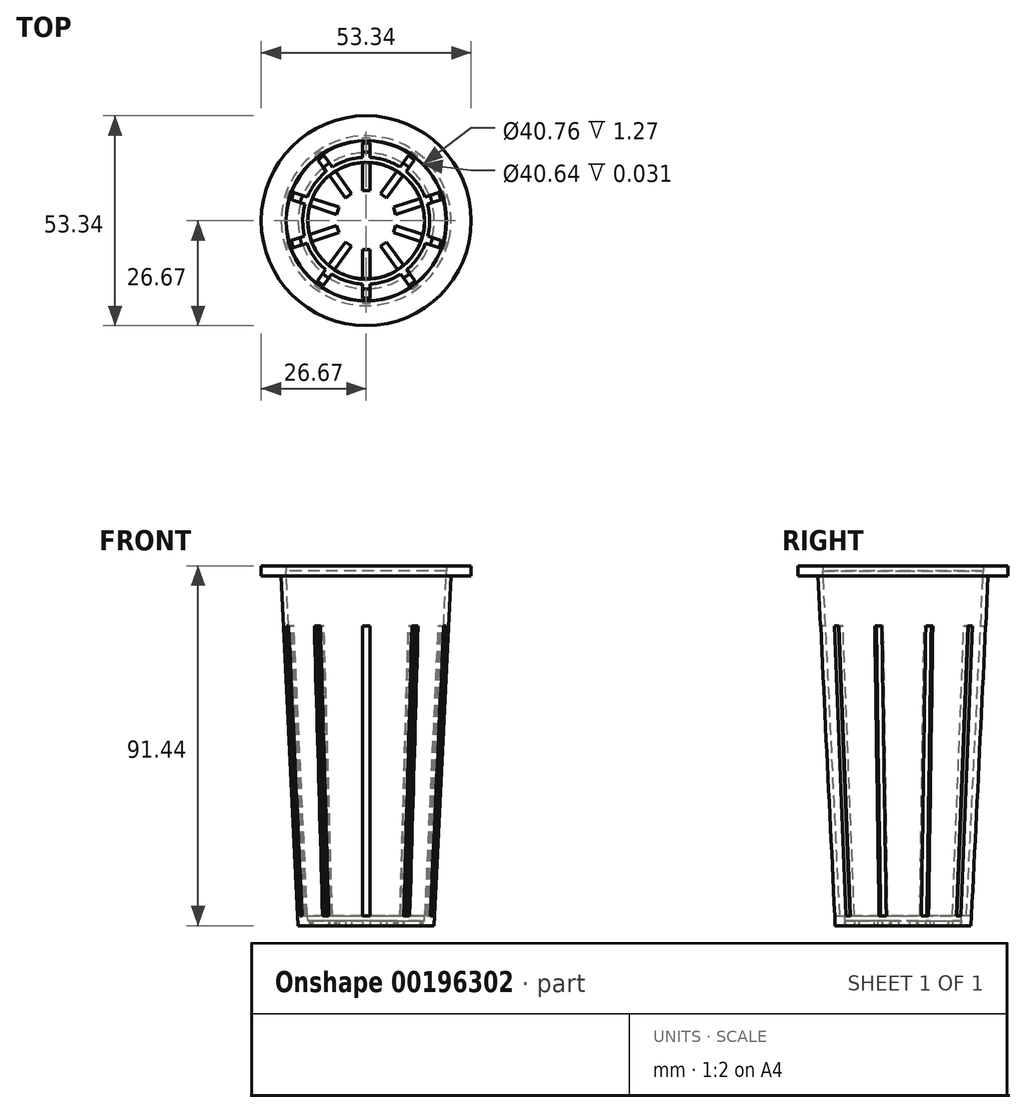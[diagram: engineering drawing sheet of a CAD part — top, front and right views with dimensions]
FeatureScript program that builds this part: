
annotation { "Feature Type Name" : "Feature", "Feature Type Description" : "" }
export const myFeature = defineFeature(function(context is Context, id is Id, definition is map)
    precondition{}
    {
        {
            var Q0;
            Q0=qCreatedBy(makeId("Front.planeOp"),FACE);
            var sketch = newSketch(context, id + "F0", { "sketchPlane" : qUnion([Q0])});
            skLineSegment(sketch, "E0", {"start": v(0, 0) * mm, "end": v(0, 88.9) * mm});
            skLineSegment(sketch, "E1", {"start": v(0, 88.9) * mm, "end": v(0, 91.44) * mm});
            skLineSegment(sketch, "E2", {"start": v(0, 91.44) * mm, "end": v(26.67, 91.44) * mm});
            skLineSegment(sketch, "E3", {"start": v(26.67, 91.44) * mm, "end": v(26.67, 88.9) * mm});
            skLineSegment(sketch, "E4", {"start": v(26.67, 88.9) * mm, "end": v(0, 88.9) * mm});
            skLineSegment(sketch, "E5", {"start": v(0, 88.9) * mm, "end": v(21.59, 88.9) * mm});
            skLineSegment(sketch, "E6", {"start": v(0, 0) * mm, "end": v(17.27, 0) * mm});
            skLineSegment(sketch, "E7", {"start": v(17.27, 0) * mm, "end": v(21.6, 88.9) * mm});
            skLineSegment(sketch, "E8", {"start": v(0, 0) * mm, "end": v(0, 2.54) * mm});
            skLineSegment(sketch, "E9", {"start": v(17.27, 0) * mm, "end": v(14.73, 0) * mm});
            skLineSegment(sketch, "E10", {"start": v(0, 2.54) * mm, "end": v(17.4, 2.54) * mm});
            skSolve(sketch);
        }
        {
            var Q0;
            Q0=qSketchRegion(id+"F0",true);
            var Q1;
            Q1=sQuery(id+"F0.wireOp",EDGE,"E0");
            revolve(context, id + "F1", {"entities" : qUnion([Q0]), "axis" : qUnion([Q1]), "revolveType" : RevolveType.FULL});
        }
        {
            var Q0;
            Q0=makeQuery(id+"F1.opRevolve","SWEPT_FACE",FACE,{"disambiguationData":[OSD([sQuery(id+"F0.wireOp",EDGE,"E2")])]});
            shell(context, id + "F2", {"entities" : qUnion([Q0]), "thickness" : 1.27 * mm});
        }
        {
            var Q0;
            Q0=makeQuery(id+"F2.opShell","OFFSET_FACE",FACE,{"disambiguationData":[OSD([sQuery(id+"F0.wireOp",EDGE,"E4")])]});
            extrude(context, id + "F3", {"entities" : qUnion([Q0]), "operationType" : NewBodyOperationType.ADD, "depth" : 1.27 * mm});
        }
        {
            var Q0;
            Q0=qCreatedBy(makeId("Top.planeOp"),FACE);
            cPlane(context, id + "F4", {"entities" : qUnion([Q0]), "cplaneType" : CPlaneType.OFFSET, "offset" : 88.9 * mm, "width" : 152.4 * mm, "height" : 152.4 * mm});
        }
        {
            var Q0;
            Q0=qCreatedBy(id+"F4.planeOp",FACE);
            var sketch = newSketch(context, id + "F5", { "sketchPlane" : qUnion([Q0])});
            skCircle(sketch, "E11", {"center": v(0, 0) * mm, "radius": 20.32 * mm});
            skSolve(sketch);
        }
        {
            var Q0;
            Q0=qSketchRegion(id+"F5",true);
            extrude(context, id + "F6", {"entities" : qUnion([Q0]), "operationType" : NewBodyOperationType.REMOVE, "depth" : 25.4 * mm});
        }
        {
            var Q0;
            Q0=qCreatedBy(makeId("Top.planeOp"),FACE);
            var sketch = newSketch(context, id + "F7", { "sketchPlane" : qUnion([Q0])});
            skLineSegment(sketch, "E12", {"start": v(0, 0) * mm, "end": v(0, -17.27) * mm});
            skLineSegment(sketch, "E13.bottom", {"start": v(0.95, -7.37) * mm, "end": v(-0.95, -7.37) * mm});
            skLineSegment(sketch, "E13.top", {"start": v(0.95, -27.18) * mm, "end": v(-0.95, -27.18) * mm});
            skLineSegment(sketch, "E13.left", {"start": v(0.95, -7.37) * mm, "end": v(0.95, -27.18) * mm});
            skLineSegment(sketch, "E13.right", {"start": v(-0.95, -7.37) * mm, "end": v(-0.95, -27.18) * mm});
            skPoint(sketch, "E13.middle", {"position": v(0, -17.27) * mm});
            skLineSegment(sketch, "E14.1.0", {"start": v(3.67, -6.48) * mm, "end": v(15.31, -22.51) * mm});
            skLineSegment(sketch, "E14.1.1", {"start": v(5.2, -5.36) * mm, "end": v(16.85, -21.4) * mm});
            skLineSegment(sketch, "E14.1.2", {"start": v(5.2, -5.36) * mm, "end": v(3.67, -6.48) * mm});
            skLineSegment(sketch, "E14.1.3", {"start": v(16.85, -21.4) * mm, "end": v(15.31, -22.51) * mm});
            skLineSegment(sketch, "E14.2.0", {"start": v(6.88, -3.06) * mm, "end": v(25.73, -9.18) * mm});
            skLineSegment(sketch, "E14.2.1", {"start": v(7.47, -1.24) * mm, "end": v(26.31, -7.37) * mm});
            skLineSegment(sketch, "E14.2.2", {"start": v(7.47, -1.24) * mm, "end": v(6.88, -3.06) * mm});
            skLineSegment(sketch, "E14.2.3", {"start": v(26.31, -7.37) * mm, "end": v(25.73, -9.18) * mm});
            skLineSegment(sketch, "E14.3.0", {"start": v(7.47, 1.6) * mm, "end": v(26.31, 7.73) * mm});
            skLineSegment(sketch, "E14.3.1", {"start": v(6.88, 3.42) * mm, "end": v(25.73, 9.54) * mm});
            skLineSegment(sketch, "E14.3.2", {"start": v(6.88, 3.42) * mm, "end": v(7.47, 1.6) * mm});
            skLineSegment(sketch, "E14.3.3", {"start": v(25.73, 9.54) * mm, "end": v(26.31, 7.73) * mm});
            skLineSegment(sketch, "E14.4.0", {"start": v(5.2, 5.73) * mm, "end": v(16.85, 21.76) * mm});
            skLineSegment(sketch, "E14.4.1", {"start": v(3.67, 6.85) * mm, "end": v(15.31, 22.88) * mm});
            skLineSegment(sketch, "E14.4.2", {"start": v(3.67, 6.85) * mm, "end": v(5.2, 5.73) * mm});
            skLineSegment(sketch, "E14.4.3", {"start": v(15.31, 22.88) * mm, "end": v(16.85, 21.76) * mm});
            skLineSegment(sketch, "E14.5.0", {"start": v(0.95, 7.73) * mm, "end": v(0.95, 27.54) * mm});
            skLineSegment(sketch, "E14.5.1", {"start": v(-0.95, 7.73) * mm, "end": v(-0.95, 27.54) * mm});
            skLineSegment(sketch, "E14.5.2", {"start": v(-0.95, 7.73) * mm, "end": v(0.95, 7.73) * mm});
            skLineSegment(sketch, "E14.5.3", {"start": v(-0.95, 27.54) * mm, "end": v(0.95, 27.54) * mm});
            skLineSegment(sketch, "E14.6.0", {"start": v(-3.67, 6.85) * mm, "end": v(-15.31, 22.88) * mm});
            skLineSegment(sketch, "E14.6.1", {"start": v(-5.2, 5.73) * mm, "end": v(-16.85, 21.76) * mm});
            skLineSegment(sketch, "E14.6.2", {"start": v(-5.2, 5.73) * mm, "end": v(-3.67, 6.85) * mm});
            skLineSegment(sketch, "E14.6.3", {"start": v(-16.85, 21.76) * mm, "end": v(-15.31, 22.88) * mm});
            skLineSegment(sketch, "E14.7.0", {"start": v(-6.88, 3.42) * mm, "end": v(-25.73, 9.54) * mm});
            skLineSegment(sketch, "E14.7.1", {"start": v(-7.47, 1.6) * mm, "end": v(-26.31, 7.73) * mm});
            skLineSegment(sketch, "E14.7.2", {"start": v(-7.47, 1.6) * mm, "end": v(-6.88, 3.42) * mm});
            skLineSegment(sketch, "E14.7.3", {"start": v(-26.31, 7.73) * mm, "end": v(-25.73, 9.54) * mm});
            skLineSegment(sketch, "E14.8.0", {"start": v(-7.47, -1.24) * mm, "end": v(-26.31, -7.37) * mm});
            skLineSegment(sketch, "E14.8.1", {"start": v(-6.88, -3.06) * mm, "end": v(-25.73, -9.18) * mm});
            skLineSegment(sketch, "E14.8.2", {"start": v(-6.88, -3.06) * mm, "end": v(-7.47, -1.24) * mm});
            skLineSegment(sketch, "E14.8.3", {"start": v(-25.73, -9.18) * mm, "end": v(-26.31, -7.37) * mm});
            skLineSegment(sketch, "E14.9.0", {"start": v(-5.2, -5.36) * mm, "end": v(-16.85, -21.4) * mm});
            skLineSegment(sketch, "E14.9.1", {"start": v(-3.67, -6.48) * mm, "end": v(-15.31, -22.51) * mm});
            skLineSegment(sketch, "E14.9.2", {"start": v(-3.67, -6.48) * mm, "end": v(-5.2, -5.36) * mm});
            skLineSegment(sketch, "E14.9.3", {"start": v(-15.31, -22.51) * mm, "end": v(-16.85, -21.4) * mm});
            skPoint(sketch, "E14.center", {"position": v(0, 0.18) * mm});
            skSolve(sketch);
        }
        {
            var Q0;
            Q0=qSketchRegion(id+"F7",true);
            extrude(context, id + "F8", {"entities" : qUnion([Q0]), "operationType" : NewBodyOperationType.REMOVE, "depth" : 76.2 * mm});
        }
        {
            var Q0;
            Q0=qCreatedBy(makeId("Front.planeOp"),FACE);
            var sketch = newSketch(context, id + "F9", { "sketchPlane" : qUnion([Q0])});
            skLineSegment(sketch, "E15", {"start": v(0, 0) * mm, "end": v(17.27, 0) * mm});
            skLineSegment(sketch, "E16", {"start": v(0, 0) * mm, "end": v(0, 2.54) * mm});
            skLineSegment(sketch, "E17", {"start": v(17.27, 0) * mm, "end": v(14.73, 0) * mm});
            skLineSegment(sketch, "E18", {"start": v(17.4, 2.54) * mm, "end": v(17.27, 0) * mm});
            skLineSegment(sketch, "E19", {"start": v(14.73, 0) * mm, "end": v(14.86, 2.54) * mm});
            skLineSegment(sketch, "E20", {"start": v(14.86, 2.54) * mm, "end": v(17.4, 2.54) * mm});
            skSolve(sketch);
        }
        {
            var Q0;
            Q0 = qSketchRegion(id + "F9", true);
            var Q1;
            Q1=sQuery(id+"F9.wireOp",EDGE,"E16");
            revolve(context, id + "F10", {"operationType" : NewBodyOperationType.ADD, "entities" : qUnion([Q0]), "axis" : qUnion([Q1]), "revolveType" : RevolveType.FULL});
        }
    });
